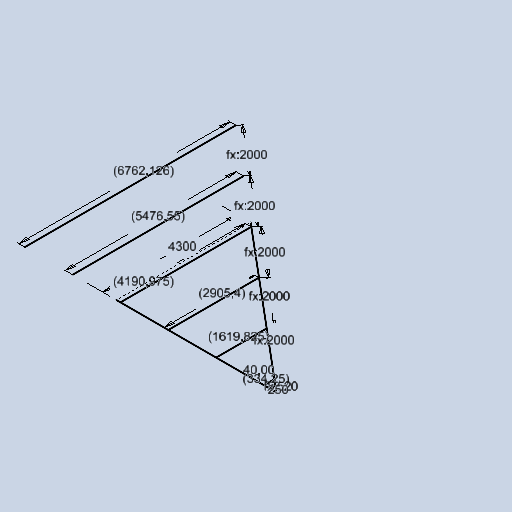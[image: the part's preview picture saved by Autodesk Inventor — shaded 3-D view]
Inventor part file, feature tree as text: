
AUTODESK INVENTOR PART (.ipt)
format: ipt  version: 2025 (Build 290162010, 162A)  size: 154,624 bytes
history: native  units: mm
features: sketch x1
ambient origin geometry x8: Origin, YZ Plane, XZ Plane, XY Plane, X Axis, Y Axis, Z Axis, Center Point
feature tree (1):
  sketch  "Sketch2"  dims[d2=6.981317mm d3=4300.0mm d6=334.249557mm d7=250.0mm d8=520.0mm d12=1837.151267mm d13=2905.399996mm d14=5476.550435mm d15=6762.125654mm d16=2000.0mm d17=2000.0mm d18=2000.0mm d19=2000.0mm d20=2000.0mm d21=1619.824776mm d22=4190.975215mm]
